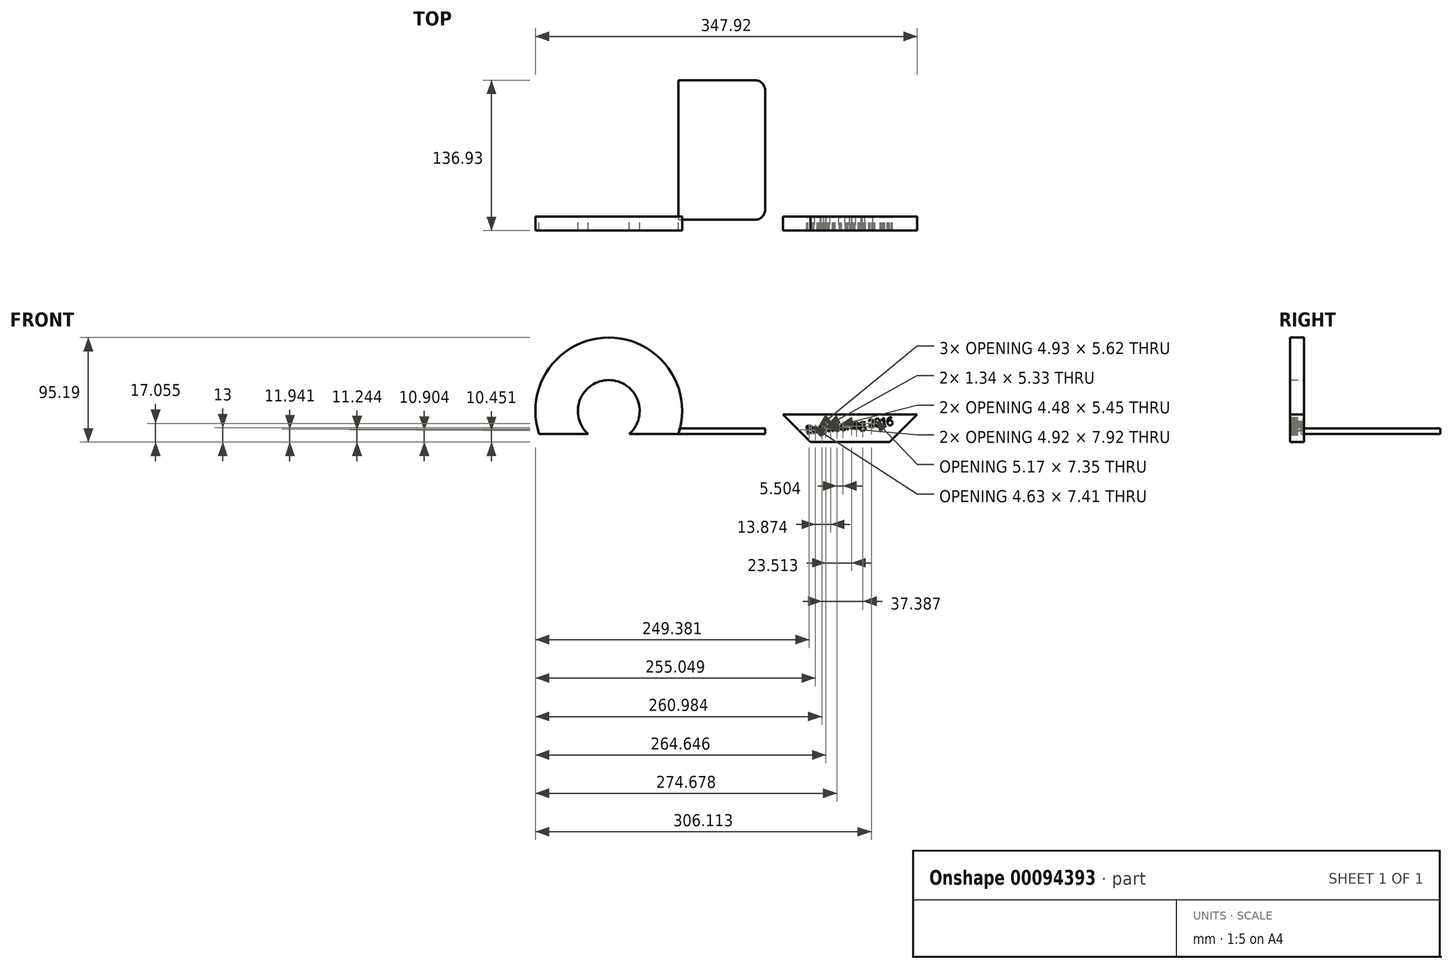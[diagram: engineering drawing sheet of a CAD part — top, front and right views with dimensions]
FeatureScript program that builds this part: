
annotation { "Feature Type Name" : "Feature", "Feature Type Description" : "" }
export const myFeature = defineFeature(function(context is Context, id is Id, definition is map)
    precondition{}
    {
        {
            var Q0;
            Q0=qCreatedBy(makeId("Top.planeOp"),FACE);
            var sketch = newSketch(context, id + "F0", { "sketchPlane" : qUnion([Q0])});
            skLineSegment(sketch, "E0.bottom", {"start": v(0, 124.23) * mm, "end": v(70.01, 124.23) * mm});
            skLineSegment(sketch, "E0.top", {"start": v(0, -2.77) * mm, "end": v(70.01, -2.77) * mm});
            skLineSegment(sketch, "E0.left", {"start": v(0, 124.23) * mm, "end": v(0, -2.77) * mm});
            skLineSegment(sketch, "E0.right", {"start": v(78.9, 115.34) * mm, "end": v(78.9, 6.12) * mm});
            skPoint(sketch, "E1.visualSharp", {"position": v(78.9, 124.23) * mm});
            skArc(sketch, "E1.filletArc", {"start": v(78.9, 115.34) * mm, "mid": v(76.3, 121.63) * mm, "end": v(70.01, 124.23) * mm});
            skPoint(sketch, "E2.visualSharp", {"position": v(78.9, -2.77) * mm});
            skArc(sketch, "E2.filletArc", {"start": v(70.01, -2.77) * mm, "mid": v(76.3, -0.17) * mm, "end": v(78.9, 6.12) * mm});
            skSolve(sketch);
        }
        {
            var Q0;
            Q0 = qSketchRegion(id + "F0", true);
            extrude(context, id + "F1", {"entities" : qUnion([Q0]), "depth" : 5.08 * mm});
        }
        {
            var Q0;
            Q0=qCreatedBy(makeId("Front.planeOp"),FACE);
            var sketch = newSketch(context, id + "F2", { "sketchPlane" : qUnion([Q0])});
            skArc(sketch, "E3", {"start": v(0, 0) * mm, "mid": v(-63.5, 87.75) * mm, "end": v(-127, 0) * mm});
            skLineSegment(sketch, "E4", {"start": v(-127, 0) * mm, "end": v(0, 0) * mm});
            skArc(sketch, "E5", {"start": v(-44.66, 0) * mm, "mid": v(-63.5, 49.03) * mm, "end": v(-82.34, 0) * mm});
            skLineSegment(sketch, "E6", {"start": v(-82.34, 0) * mm, "end": v(-44.66, 0) * mm});
            skSolve(sketch);
        }
        {
            var Q0;
            {var subQ0=sQuery(id+"F2.wireOp",EDGE,"E3");Q0=makeQuery(id+"F2.imprint","IMPRINT",FACE,{"disambiguationData":[TD([[makeQuery(id+"F2.imprint","IMPRINT",EDGE,{"derivedFrom":subQ0}),1.0]])]});}
            extrude(context, id + "F3", {"entities" : qUnion([Q0]), "depth" : 12.7 * mm});
        }
        {
            var Q0;
            Q0=qCreatedBy(makeId("Front.planeOp"),FACE);
            var sketch = newSketch(context, id + "F4", { "sketchPlane" : qUnion([Q0])});
            skText(sketch, "E7", { "text": "Engineering 2016\n", "fontName": "OpenSans-Regular.ttf"});
            skLineSegment(sketch, "E8.bottom", {"start": v(120.3, 17.68) * mm, "end": v(217.57, 17.68) * mm});
            skLineSegment(sketch, "E8.top", {"start": v(120.3, -7.44) * mm, "end": v(192.45, -7.44) * mm});
            skLineSegment(sketch, "E9.bottom", {"start": v(217.57, 17.68) * mm, "end": v(205.1, 17.68) * mm});
            skLineSegment(sketch, "E10.bottom", {"start": v(217.57, 17.68) * mm, "end": v(192.45, 17.68) * mm});
            skLineSegment(sketch, "E11", {"start": v(192.45, -7.44) * mm, "end": v(217.57, 17.68) * mm});
            skLineSegment(sketch, "E12.top", {"start": v(120.3, 17.69) * mm, "end": v(95.17, 17.69) * mm});
            skLineSegment(sketch, "E12.left", {"start": v(120.3, 17.68) * mm, "end": v(120.3, 17.69) * mm});
            skLineSegment(sketch, "E13", {"start": v(120.3, -7.44) * mm, "end": v(95.17, 17.69) * mm});
            const initialGuessF4  = {"E7": [0.11648, 0, 0.99466, 0.1032, 0.0071]};
            skSetInitialGuess(sketch, initialGuessF4);
            skSolve(sketch);
        }
        {
            var Q0;
            Q0 = qSketchRegion(id + "F4", true);
            extrude(context, id + "F5", {"entities" : qUnion([Q0]), "depth" : 12.7 * mm});
        }
    });
